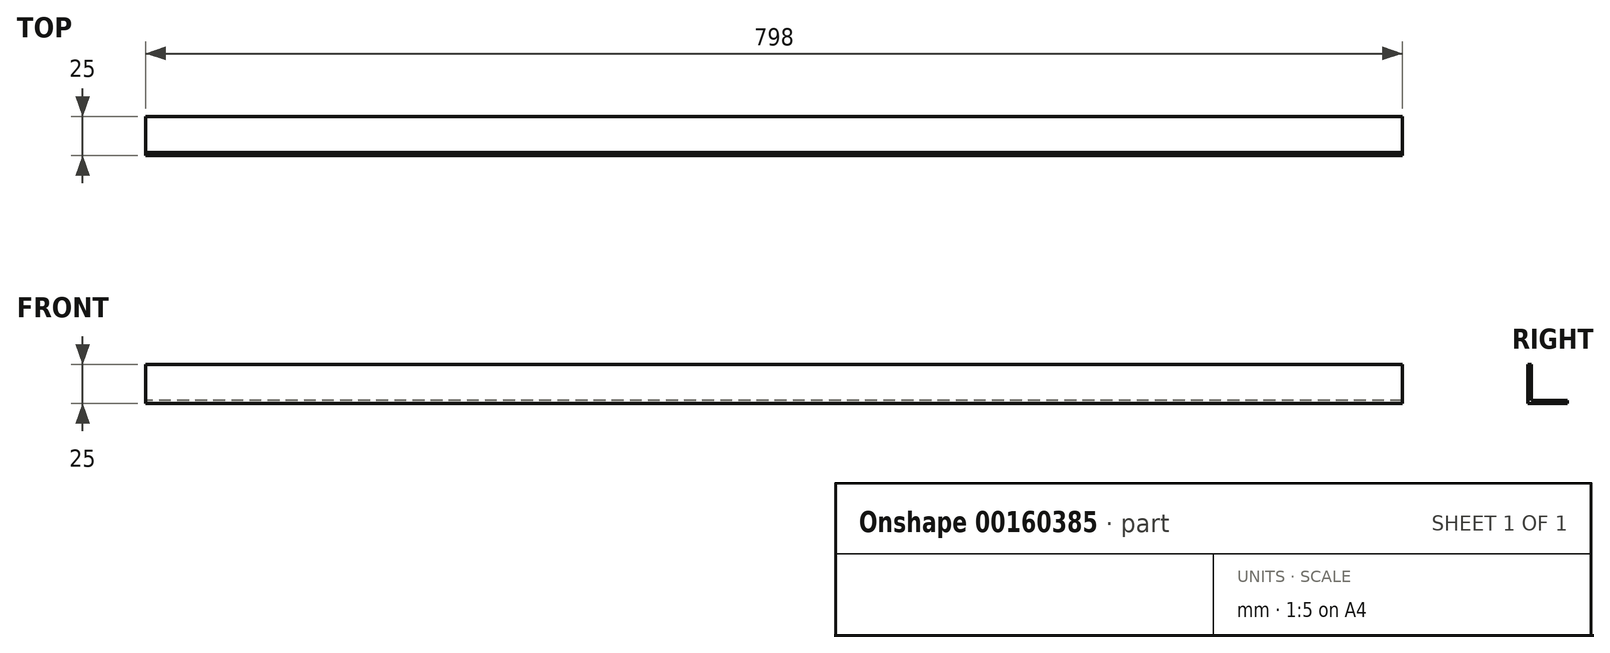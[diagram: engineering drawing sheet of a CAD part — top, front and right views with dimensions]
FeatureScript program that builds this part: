
annotation { "Feature Type Name" : "Feature", "Feature Type Description" : "" }
export const myFeature = defineFeature(function(context is Context, id is Id, definition is map)
    precondition{}
    {
        {
            var Q0;
            Q0=qCreatedBy(makeId("Right.planeOp"),FACE);
            var sketch = newSketch(context, id + "F0", { "sketchPlane" : qUnion([Q0])});
            skLineSegment(sketch, "E0", {"start": v(0, 0) * mm, "end": v(-25, 0) * mm});
            skLineSegment(sketch, "E1", {"start": v(-25, 0) * mm, "end": v(-25, 25) * mm});
            skLineSegment(sketch, "E2", {"start": v(-25, 25) * mm, "end": v(-23, 25) * mm});
            skLineSegment(sketch, "E3", {"start": v(-23, 25) * mm, "end": v(-23, 2) * mm});
            skLineSegment(sketch, "E4", {"start": v(-23, 2) * mm, "end": v(0, 2) * mm});
            skLineSegment(sketch, "E5", {"start": v(0, 2) * mm, "end": v(0, 0) * mm});
            skSolve(sketch);
        }
        {
            var Q0;
            Q0=qSketchRegion(id+"F0",true);
            extrude(context, id + "F1", {"entities" : qUnion([Q0]), "depth" : 798 * mm});
        }
    });
